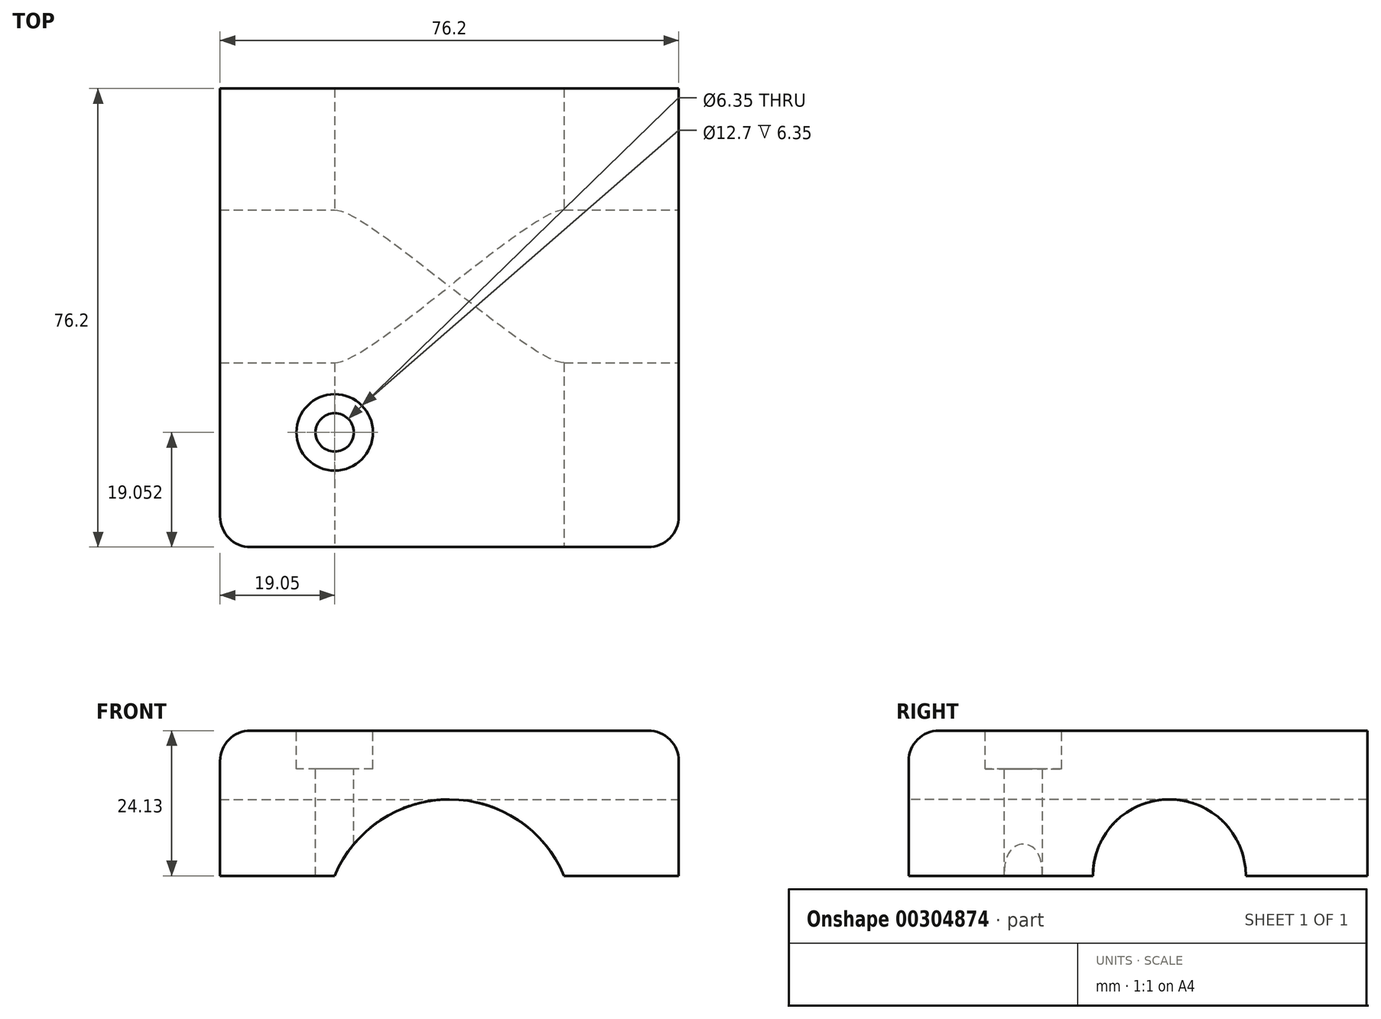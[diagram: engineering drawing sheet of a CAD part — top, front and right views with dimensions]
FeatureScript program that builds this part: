
annotation { "Feature Type Name" : "Feature", "Feature Type Description" : "" }
export const myFeature = defineFeature(function(context is Context, id is Id, definition is map)
    precondition{}
    {
        {
            var Q0;
            Q0=qCreatedBy(makeId("Top.planeOp"),FACE);
            var sketch = newSketch(context, id + "F0", { "sketchPlane" : qUnion([Q0])});
            skLineSegment(sketch, "E0.bottom", {"start": v(-76.2, 21.22) * mm, "end": v(0, 21.22) * mm});
            skLineSegment(sketch, "E0.top", {"start": v(-76.2, -54.98) * mm, "end": v(0, -54.98) * mm});
            skLineSegment(sketch, "E0.left", {"start": v(-76.2, 21.22) * mm, "end": v(-76.2, -54.98) * mm});
            skLineSegment(sketch, "E0.right", {"start": v(0, 21.22) * mm, "end": v(0, -54.98) * mm});
            skSolve(sketch);
        }
        {
            var Q0;
            Q0=makeQuery(id+"F0.imprint","IMPRINT",FACE,{"disambiguationData":[TD([[makeQuery(id+"F0.imprint","IMPRINT",EDGE,{"derivedFrom":sQuery(id+"F0.wireOp",EDGE,"E0.bottom")}),-1.0]])]});
            extrude(context, id + "F1", {"entities" : qUnion([Q0]), "depth" : 24.13 * mm});
        }
        {
            var Q0;
            Q0=makeQuery(id+"F1.opExtrude","SWEPT_FACE",FACE,{"disambiguationData":[OSD([sQuery(id+"F0.wireOp",EDGE,"E0.right")])]});
            var sketch = newSketch(context, id + "F2", { "sketchPlane" : qUnion([Q0])});
            skCircle(sketch, "E1", {"center": v(-11.67, 0) * mm, "radius": 12.7 * mm});
            skSolve(sketch);
        }
        {
            var Q0;
            {var subQ0=sQuery(id+"F2.wireOp",EDGE,"E1");var subQ1=makeQuery(id+"F1.opExtrude","CAP_EDGE",EDGE,{"disambiguationData":[OSD([sQuery(id+"F0.wireOp",EDGE,"E0.right")])],"isStart":true});var subQ2=makeQuery(id+"F2.imprint","INTERSECT",VERTEX,{"disambiguationData":[OD(0.0)],"derivedFrom":[subQ1,subQ0]});Q0=makeQuery(id+"F2.imprint","IMPRINT",FACE,{"disambiguationData":[TD([[makeQuery(id+"F2.imprint","IMPRINT",EDGE,{"disambiguationData":[TD([[subQ2,-1.0]])],"derivedFrom":subQ0}),1.0]])]});}
            extrude(context, id + "F3", {"entities" : qUnion([Q0]), "operationType" : NewBodyOperationType.REMOVE, "endBound" : BoundingType.THROUGH_ALL, "oppositeDirection" : true, "depth" : 25.4 * mm});
        }
        {
            var Q0;
            Q0=makeQuery(id+"F1.opExtrude","SWEPT_FACE",FACE,{"disambiguationData":[OSD([sQuery(id+"F0.wireOp",EDGE,"E0.top")])]});
            var sketch = newSketch(context, id + "F4", { "sketchPlane" : qUnion([Q0])});
            skLineSegment(sketch, "E2.bottom", {"start": v(-76.2, 0) * mm, "end": v(-57.15, 0) * mm, "construction": true});
            skLineSegment(sketch, "E2.top", {"start": v(-76.2, 9.94) * mm, "end": v(-57.15, 9.94) * mm, "construction": true});
            skLineSegment(sketch, "E2.left", {"start": v(-76.2, 0) * mm, "end": v(-76.2, 9.94) * mm, "construction": true});
            skLineSegment(sketch, "E2.right", {"start": v(-57.15, 0) * mm, "end": v(-57.15, 9.94) * mm, "construction": true});
            skLineSegment(sketch, "E3.bottom", {"start": v(0, 0) * mm, "end": v(-19.05, 0) * mm});
            skLineSegment(sketch, "E3.top", {"start": v(0, 7.81) * mm, "end": v(-19.05, 7.81) * mm});
            skLineSegment(sketch, "E3.left", {"start": v(0, 0) * mm, "end": v(0, 7.81) * mm});
            skLineSegment(sketch, "E3.right", {"start": v(-19.05, 0) * mm, "end": v(-19.05, 7.81) * mm});
            skLineSegment(sketch, "E4.bottom", {"start": v(-38.1, 0) * mm, "end": v(-25.2, 0) * mm, "construction": true});
            skLineSegment(sketch, "E4.top", {"start": v(-38.1, 12.7) * mm, "end": v(-25.2, 12.7) * mm, "construction": true});
            skLineSegment(sketch, "E4.left", {"start": v(-38.1, 0) * mm, "end": v(-38.1, 12.7) * mm, "construction": true});
            skLineSegment(sketch, "E4.right", {"start": v(-25.2, 0) * mm, "end": v(-25.2, 12.7) * mm, "construction": true});
            skArc(sketch, "E5", {"start": v(-19.05, 0) * mm, "mid": v(-38.1, 12.7) * mm, "end": v(-57.15, 0) * mm});
            skSolve(sketch);
        }
        {
            var Q0;
            {var subQ0=sQuery(id+"F4.wireOp",EDGE,"E5");Q0=makeQuery(id+"F4.imprint","IMPRINT",FACE,{"disambiguationData":[TD([[makeQuery(id+"F4.imprint","IMPRINT",EDGE,{"derivedFrom":subQ0}),1.0]])]});}
            extrude(context, id + "F5", {"entities" : qUnion([Q0]), "operationType" : NewBodyOperationType.REMOVE, "endBound" : BoundingType.THROUGH_ALL, "oppositeDirection" : true, "depth" : 25.4 * mm});
        }
        {
            var Q0;
            Q0=makeQuery(id+"F1.opExtrude","CAP_FACE",FACE,{"disambiguationData":[OSD([sQuery(id+"F0.wireOp",EDGE,"E0.bottom"),sQuery(id+"F0.wireOp",EDGE,"E0.top"),sQuery(id+"F0.wireOp",EDGE,"E0.left"),sQuery(id+"F0.wireOp",EDGE,"E0.right")])],"isStart":false});
            var sketch = newSketch(context, id + "F6", { "sketchPlane" : qUnion([Q0])});
            skLineSegment(sketch, "E6.bottom", {"start": v(-76.2, -54.98) * mm, "end": v(-57.15, -54.98) * mm, "construction": true});
            skLineSegment(sketch, "E6.top", {"start": v(-76.2, -35.93) * mm, "end": v(-57.15, -35.93) * mm, "construction": true});
            skLineSegment(sketch, "E6.left", {"start": v(-76.2, -54.98) * mm, "end": v(-76.2, -35.93) * mm, "construction": true});
            skLineSegment(sketch, "E6.right", {"start": v(-57.15, -54.98) * mm, "end": v(-57.15, -35.93) * mm, "construction": true});
            skCircle(sketch, "E7", {"center": v(-57.15, -35.93) * mm, "radius": 3.18 * mm, "construction": true});
            skSolve(sketch);
        }
        {
            var Q0;
            Q0=sQuery(id+"F6.wireOp",VERTEX,"E6.right.end");
            var Q1;
            Q1=makeQuery(id+"F1.opExtrude","SWEPT_BODY",BODY,{"disambiguationData":[OSD([sQuery(id+"F0.wireOp",EDGE,"E0.bottom"),sQuery(id+"F0.wireOp",EDGE,"E0.top"),sQuery(id+"F0.wireOp",EDGE,"E0.left"),sQuery(id+"F0.wireOp",EDGE,"E0.right")])]});
            hole(context, id + "F7", {"style" : HoleStyle.C_BORE, "endStyle" : HoleEndStyle.THROUGH, "holeDiameter" : 6.35 * mm, "cBoreDiameter" : 12.7 * mm, "cBoreDepth" : 6.35 * mm, "tappedDepth" : 12.7 * mm, "tapClearance" : 3, "locations" : qUnion([Q0]), "scope" : qUnion([Q1])});
        }
        {
            var Q0;
            Q0=makeQuery(id+"F1.opExtrude","CAP_EDGE",EDGE,{"disambiguationData":[OSD([sQuery(id+"F0.wireOp",EDGE,"E0.left")])],"isStart":false});
            fillet(context, id + "F8", {"entities" : qUnion([Q0]), "radius" : 5.08 * mm, "tangentPropagation" : true, "allowEdgeOverflow" : false});
        }
        {
            var Q0;
            Q0=makeQuery(id+"F1.opExtrude","CAP_EDGE",EDGE,{"disambiguationData":[OSD([sQuery(id+"F0.wireOp",EDGE,"E0.top")])],"isStart":false});
            fillet(context, id + "F9", {"entities" : qUnion([Q0]), "radius" : 5.08 * mm, "tangentPropagation" : true, "allowEdgeOverflow" : false});
        }
        {
            var Q0;
            Q0=makeQuery(id+"F1.opExtrude","CAP_EDGE",EDGE,{"disambiguationData":[OSD([sQuery(id+"F0.wireOp",EDGE,"E0.right")])],"isStart":false});
            fillet(context, id + "F10", {"entities" : qUnion([Q0]), "radius" : 5.08 * mm, "tangentPropagation" : true, "allowEdgeOverflow" : false});
        }
    });
